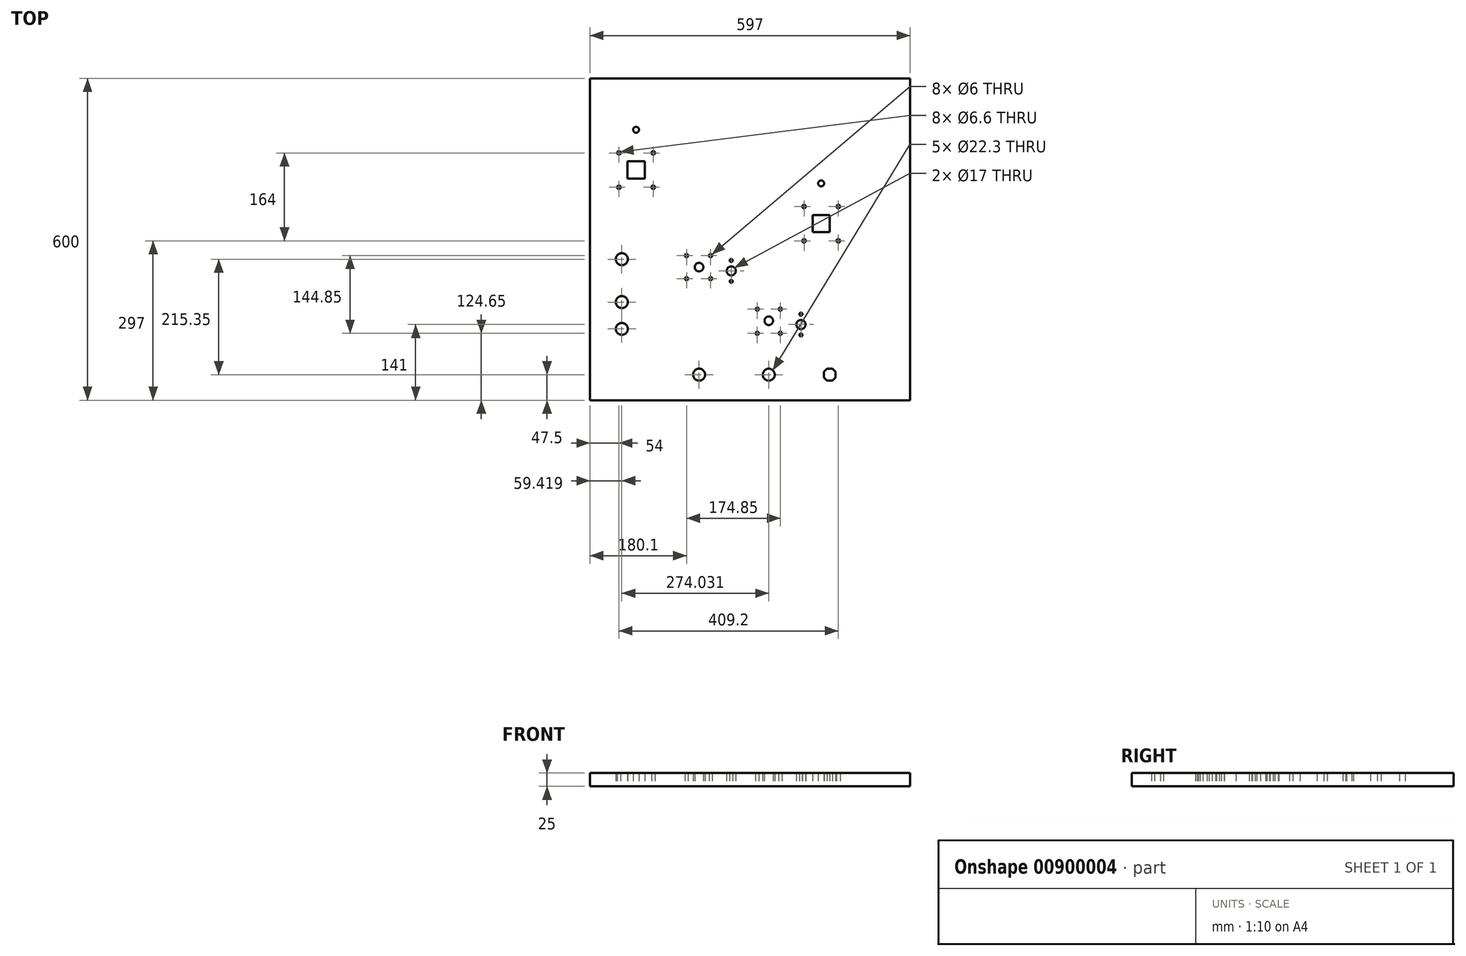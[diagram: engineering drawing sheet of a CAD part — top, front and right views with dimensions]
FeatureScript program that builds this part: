
annotation { "Feature Type Name" : "Feature", "Feature Type Description" : "" }
export const myFeature = defineFeature(function(context is Context, id is Id, definition is map)
    precondition{}
    {
        {
            var Q0;
            Q0=qCreatedBy(makeId("Top.planeOp"),FACE);
            var sketch = newSketch(context, id + "F0", { "sketchPlane" : qUnion([Q0])});
            skLineSegment(sketch, "E0", {"start": v(159.5, -257.76) * mm, "end": v(159.5, -247.24) * mm});
            skLineSegment(sketch, "E1", {"start": v(153.76, -263.5) * mm, "end": v(159.5, -257.76) * mm});
            skLineSegment(sketch, "E2", {"start": v(143.24, -263.5) * mm, "end": v(153.76, -263.5) * mm});
            skLineSegment(sketch, "E3", {"start": v(137.5, -257.76) * mm, "end": v(143.24, -263.5) * mm});
            skLineSegment(sketch, "E4", {"start": v(137.5, -247.24) * mm, "end": v(137.5, -257.76) * mm});
            skLineSegment(sketch, "E5", {"start": v(143.24, -241.5) * mm, "end": v(137.5, -247.24) * mm});
            skLineSegment(sketch, "E6", {"start": v(153.76, -241.5) * mm, "end": v(143.24, -241.5) * mm});
            skLineSegment(sketch, "E7", {"start": v(159.5, -247.24) * mm, "end": v(153.76, -241.5) * mm});
            skCircle(sketch, "E8", {"center": v(132.7, 104.15) * mm, "radius": 5.5 * mm});
            skCircle(sketch, "E9", {"center": v(-212.5, 204.15) * mm, "radius": 5.5 * mm});
            skCircle(sketch, "E10", {"center": v(-239.08, -37.15) * mm, "radius": 11.15 * mm});
            skCircle(sketch, "E11", {"center": v(-239.08, -117.15) * mm, "radius": 11.15 * mm});
            skCircle(sketch, "E12", {"center": v(-239.08, -167.15) * mm, "radius": 11.15 * mm});
            skCircle(sketch, "E13", {"center": v(-95.05, -252.5) * mm, "radius": 11.15 * mm});
            skCircle(sketch, "E14", {"center": v(34.95, -252.5) * mm, "radius": 11.15 * mm});
            skCircle(sketch, "E15", {"center": v(94.95, -139.5) * mm, "radius": 2.75 * mm});
            skCircle(sketch, "E16", {"center": v(94.95, -178.5) * mm, "radius": 2.75 * mm});
            skCircle(sketch, "E17", {"center": v(-35.05, -39.5) * mm, "radius": 2.75 * mm});
            skCircle(sketch, "E18", {"center": v(-35.05, -78.5) * mm, "radius": 2.75 * mm});
            skCircle(sketch, "E19", {"center": v(94.95, -159) * mm, "radius": 8.5 * mm});
            skCircle(sketch, "E20", {"center": v(-35.05, -59) * mm, "radius": 8.5 * mm});
            skCircle(sketch, "E21", {"center": v(34.95, -152) * mm, "radius": 8 * mm});
            skCircle(sketch, "E22", {"center": v(-95.05, -52) * mm, "radius": 8 * mm});
            skCircle(sketch, "E23", {"center": v(56.45, -130.35) * mm, "radius": 3 * mm});
            skCircle(sketch, "E24", {"center": v(13.45, -130.35) * mm, "radius": 3 * mm});
            skCircle(sketch, "E25", {"center": v(56.45, -175.35) * mm, "radius": 3 * mm});
            skCircle(sketch, "E26", {"center": v(13.45, -175.35) * mm, "radius": 3 * mm});
            skCircle(sketch, "E27", {"center": v(-73.4, -30.5) * mm, "radius": 3 * mm});
            skCircle(sketch, "E28", {"center": v(-73.4, -73.5) * mm, "radius": 3 * mm});
            skCircle(sketch, "E29", {"center": v(-118.4, -30.5) * mm, "radius": 3 * mm});
            skCircle(sketch, "E30", {"center": v(-118.4, -73.5) * mm, "radius": 3 * mm});
            skCircle(sketch, "E31", {"center": v(-244.5, 97) * mm, "radius": 3.3 * mm});
            skCircle(sketch, "E32", {"center": v(-244.5, 161) * mm, "radius": 3.3 * mm});
            skCircle(sketch, "E33", {"center": v(-180.5, 97) * mm, "radius": 3.3 * mm});
            skCircle(sketch, "E34", {"center": v(-180.5, 161) * mm, "radius": 3.3 * mm});
            skCircle(sketch, "E35", {"center": v(100.7, 61) * mm, "radius": 3.3 * mm});
            skCircle(sketch, "E36", {"center": v(164.7, 61) * mm, "radius": 3.3 * mm});
            skCircle(sketch, "E37", {"center": v(164.7, -3) * mm, "radius": 3.3 * mm});
            skCircle(sketch, "E38", {"center": v(100.7, -3) * mm, "radius": 3.3 * mm});
            skLineSegment(sketch, "E39", {"start": v(-228.65, 112.85) * mm, "end": v(-196.35, 112.85) * mm});
            skLineSegment(sketch, "E40", {"start": v(-228.65, 145.15) * mm, "end": v(-228.65, 112.85) * mm});
            skLineSegment(sketch, "E41", {"start": v(-196.35, 145.15) * mm, "end": v(-228.65, 145.15) * mm});
            skLineSegment(sketch, "E42", {"start": v(-196.35, 112.85) * mm, "end": v(-196.35, 145.15) * mm});
            skLineSegment(sketch, "E43", {"start": v(148.55, 45.15) * mm, "end": v(116.55, 45.15) * mm});
            skLineSegment(sketch, "E44", {"start": v(148.55, 13.15) * mm, "end": v(148.55, 45.15) * mm});
            skLineSegment(sketch, "E45", {"start": v(116.55, 13.15) * mm, "end": v(148.55, 13.15) * mm});
            skLineSegment(sketch, "E46", {"start": v(116.55, 45.15) * mm, "end": v(116.55, 13.15) * mm});
            skLineSegment(sketch, "E47", {"start": v(-298.5, -300) * mm, "end": v(298.5, -300) * mm});
            skLineSegment(sketch, "E48", {"start": v(298.5, -300) * mm, "end": v(298.5, 300) * mm});
            skLineSegment(sketch, "E49", {"start": v(298.5, 300) * mm, "end": v(-298.5, 300) * mm});
            skLineSegment(sketch, "E50", {"start": v(-298.5, 300) * mm, "end": v(-298.5, -300) * mm});
            skSolve(sketch);
        }
        {
            var Q0;
            Q0=makeQuery(id+"F0.imprint","IMPRINT",FACE,{"disambiguationData":[TD([[makeQuery(id+"F0.imprint","IMPRINT",EDGE,{"derivedFrom":sQuery(id+"F0.wireOp",EDGE,"E0")}),-1.0]])]});
            extrude(context, id + "F1", {"entities" : qUnion([Q0]), "depth" : 25 * mm, "offsetDistance" : 25 * mm});
        }
    });
